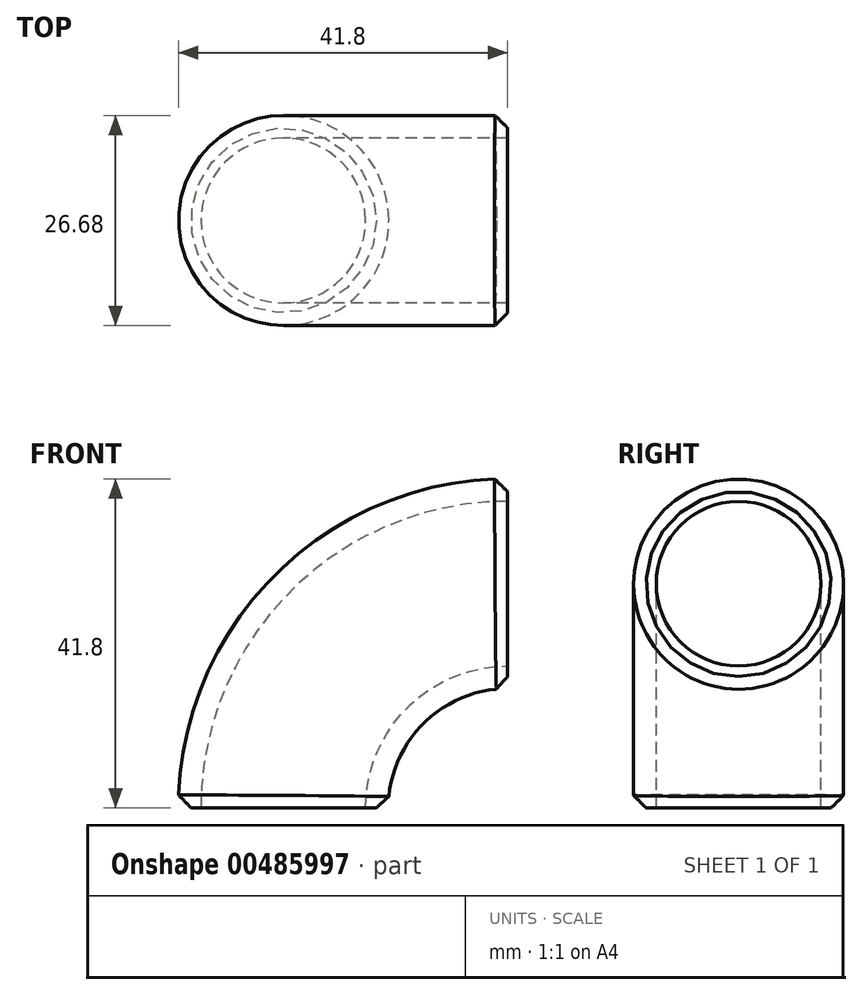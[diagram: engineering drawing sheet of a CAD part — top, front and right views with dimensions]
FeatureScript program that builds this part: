
annotation { "Feature Type Name" : "Feature", "Feature Type Description" : "" }
export const myFeature = defineFeature(function(context is Context, id is Id, definition is map)
    precondition{}
    {
        {
            var Q0;
            Q0=qCreatedBy(makeId("Top.planeOp"),FACE);
            var sketch = newSketch(context, id + "F0", { "sketchPlane" : qUnion([Q0])});
            skCircle(sketch, "E0", {"center": v(0, 0) * mm, "radius": 10.47 * mm});
            skCircle(sketch, "E1", {"center": v(0, 0) * mm, "radius": 13.34 * mm});
            skSolve(sketch);
        }
        {
            var Q0;
            Q0=qCreatedBy(makeId("Front.planeOp"),FACE);
            var sketch = newSketch(context, id + "F1", { "sketchPlane" : qUnion([Q0])});
            skLineSegment(sketch, "E2", {"start": v(0, 0) * mm, "end": v(28.5, 0) * mm, "construction": true});
            skArc(sketch, "E3", {"start": v(0, 0) * mm, "mid": v(8.35, 20.15) * mm, "end": v(28.5, 28.5) * mm});
            skLineSegment(sketch, "E4", {"start": v(28.5, 28.5) * mm, "end": v(28.5, 0) * mm, "construction": true});
            skSolve(sketch);
        }
        {
            var Q0;
            Q0=makeQuery(id+"F0.imprint","IMPRINT",FACE,{"disambiguationData":[TD([[makeQuery(id+"F0.imprint","IMPRINT",EDGE,{"derivedFrom":sQuery(id+"F0.wireOp",EDGE,"E0")}),-1.0]])]});
            var Q1;
            Q1=sQuery(id+"F1.wireOp",EDGE,"E3");
            sweep(context, id + "F2", {"profiles" : qUnion([Q0]), "path" : qUnion([Q1])});
        }
        {
            var Q0;
            Q0=makeQuery(id+"F2.opSweep","CAP_EDGE",EDGE,{"disambiguationData":[OSD([sQuery(id+"F0.wireOp",EDGE,"E1"),sQuery(id+"F1.wireOp",VERTEX,"E3.end")])],"isStart":false});
            var Q1;
            Q1=makeQuery(id+"F2.opSweep","CAP_EDGE",EDGE,{"disambiguationData":[OSD([sQuery(id+"F0.wireOp",EDGE,"E1"),sQuery(id+"F1.wireOp",VERTEX,"E3.start")])],"isStart":true});
            chamfer(context, id + "F3", {"entities" : qUnion([Q0, Q1]), "width" : 1.6 * mm, "tangentPropagation" : true});
        }
    });
